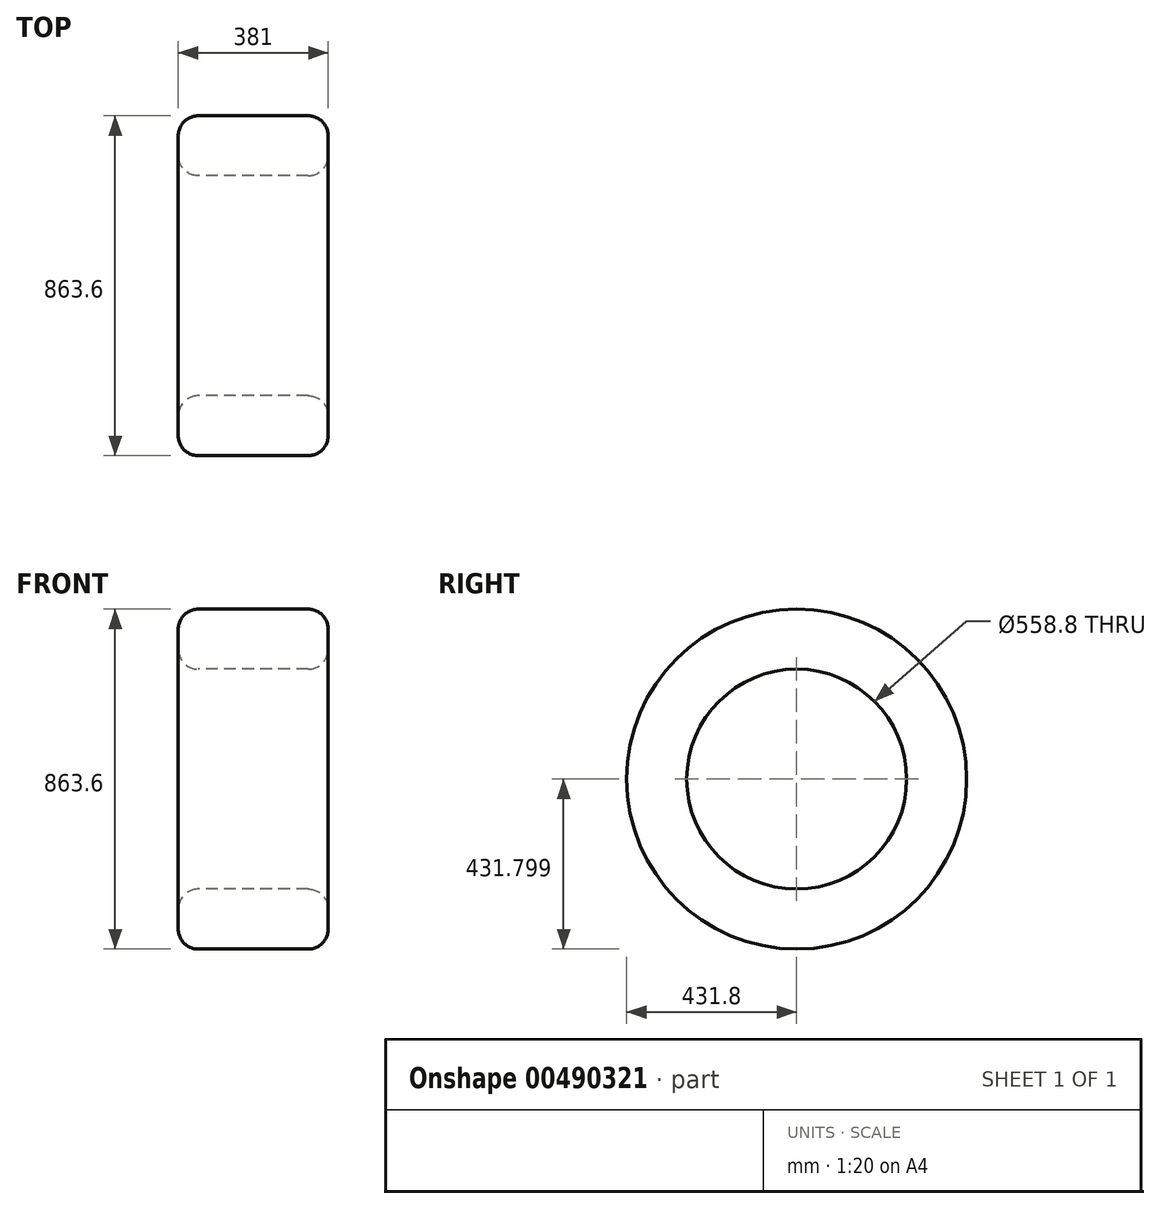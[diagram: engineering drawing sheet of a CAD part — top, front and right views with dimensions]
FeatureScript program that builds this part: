
annotation { "Feature Type Name" : "Feature", "Feature Type Description" : "" }
export const myFeature = defineFeature(function(context is Context, id is Id, definition is map)
    precondition{}
    {
        {
            var Q0;
            Q0=qCreatedBy(makeId("Front.planeOp"),FACE);
            var sketch = newSketch(context, id + "F0", { "sketchPlane" : qUnion([Q0])});
            skLineSegment(sketch, "E0.bottom", {"start": v(-154.16, 90.89) * mm, "end": v(125.24, 90.89) * mm});
            skLineSegment(sketch, "E0.top", {"start": v(-154.16, -61.51) * mm, "end": v(125.24, -61.51) * mm});
            skLineSegment(sketch, "E0.left", {"start": v(-204.96, 40.09) * mm, "end": v(-204.96, -10.71) * mm});
            skLineSegment(sketch, "E0.right", {"start": v(176.04, 40.09) * mm, "end": v(176.04, -10.71) * mm});
            skLineSegment(sketch, "E1", {"start": v(-229.06, -340.91) * mm, "end": v(152.83, -340.91) * mm});
            skPoint(sketch, "E2.visualSharp", {"position": v(-204.96, 90.89) * mm});
            skArc(sketch, "E2.filletArc", {"start": v(-154.16, 90.89) * mm, "mid": v(-190.08, 76.01) * mm, "end": v(-204.96, 40.09) * mm});
            skPoint(sketch, "E3.visualSharp", {"position": v(-204.96, -61.51) * mm});
            skArc(sketch, "E3.filletArc", {"start": v(-204.96, -10.71) * mm, "mid": v(-190.08, -46.63) * mm, "end": v(-154.16, -61.51) * mm});
            skPoint(sketch, "E4.visualSharp", {"position": v(176.04, -61.51) * mm});
            skArc(sketch, "E4.filletArc", {"start": v(125.24, -61.51) * mm, "mid": v(161.16, -46.63) * mm, "end": v(176.04, -10.71) * mm});
            skPoint(sketch, "E5.visualSharp", {"position": v(176.04, 90.89) * mm});
            skArc(sketch, "E5.filletArc", {"start": v(176.04, 40.09) * mm, "mid": v(161.16, 76.01) * mm, "end": v(125.24, 90.89) * mm});
            skSolve(sketch);
        }
        {
            var Q0;
            Q0=makeQuery(id+"F0.imprint","IMPRINT",FACE,{"disambiguationData":[TD([[makeQuery(id+"F0.imprint","IMPRINT",EDGE,{"derivedFrom":sQuery(id+"F0.wireOp",EDGE,"E0.bottom")}),-1.0]])]});
            var Q1;
            Q1=sQuery(id+"F0.wireOp",EDGE,"E1");
            revolve(context, id + "F1", {"entities" : qUnion([Q0]), "axis" : qUnion([Q1]), "revolveType" : RevolveType.FULL});
        }
    });
